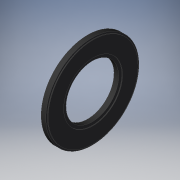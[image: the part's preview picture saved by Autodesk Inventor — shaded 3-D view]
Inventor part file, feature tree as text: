
AUTODESK INVENTOR PART (.ipt)
format: ipt  version: 2019 (Build 230136000, 136)  size: 142,336 bytes
history: native  units: mm
features: other x14, revolve x1, sketch x1
ambient origin geometry x8: Origin, YZ Plane, XZ Plane, XY Plane, X Axis, Y Axis, Z Axis, Center Point
bodies: Solid1 (feature_tree)
feature tree (16):
  revolve  "Revolution1"  [1 undecoded]
  other  "core_to_washer_XY"
  other  "core_to_washer_YZ"
  other  "core_to_washer_ZX"
  other  "core_to_washer_X"
  other  "core_to_washer_Y"
  other  "core_to_washer_Z"
  other  "core_to_washer_Center"
  other  "core_to_washer1_XY"
  other  "core_to_washer1_YZ"
  other  "core_to_washer1_ZX"
  other  "core_to_washer1_X"
  other  "core_to_washer1_Y"
  other  "core_to_washer1_Z"
  other  "core_to_washer1_Center"
  sketch  "Sketch_1"  dims[d0=360.0deg]
note: 1 required parameter value undecoded (feature->parameter linkage not recoverable at this tier; creation-order binding heuristic only, values carry confidence <= 0.55)
